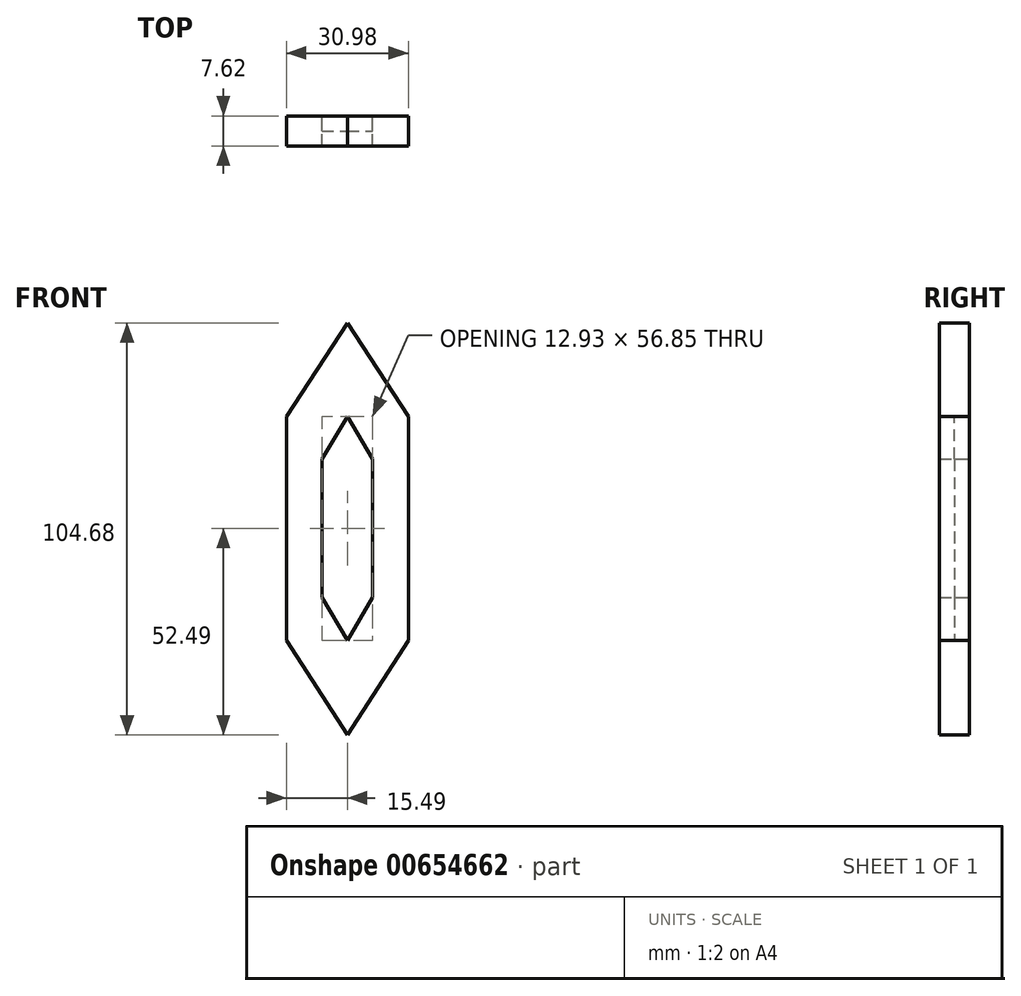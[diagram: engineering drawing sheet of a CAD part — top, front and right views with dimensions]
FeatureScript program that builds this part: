
annotation { "Feature Type Name" : "Feature", "Feature Type Description" : "" }
export const myFeature = defineFeature(function(context is Context, id is Id, definition is map)
    precondition{}
    {
        {
            var Q0;
            Q0=qCreatedBy(makeId("Front.planeOp"),FACE);
            var sketch = newSketch(context, id + "F0", { "sketchPlane" : qUnion([Q0])});
            skLineSegment(sketch, "E0.left", {"start": v(-15.5, 28.42) * mm, "end": v(-15.5, -28.42) * mm});
            skLineSegment(sketch, "E0.right", {"start": v(15.5, 28.42) * mm, "end": v(15.5, -28.42) * mm});
            skPoint(sketch, "E0.middle", {"position": v(0, 0) * mm});
            skLineSegment(sketch, "E1", {"start": v(-15.5, 28.42) * mm, "end": v(0, 52.19) * mm});
            skLineSegment(sketch, "E2", {"start": v(0, 52.19) * mm, "end": v(15.5, 28.42) * mm});
            skLineSegment(sketch, "E3", {"start": v(-15.5, -28.42) * mm, "end": v(0, -52.49) * mm});
            skLineSegment(sketch, "E4", {"start": v(0, -52.49) * mm, "end": v(15.5, -28.42) * mm});
            skLineSegment(sketch, "E5.left", {"start": v(-6.47, 17.6) * mm, "end": v(-6.47, -17.6) * mm});
            skLineSegment(sketch, "E5.right", {"start": v(6.47, 17.6) * mm, "end": v(6.47, -17.6) * mm});
            skLineSegment(sketch, "E6", {"start": v(-6.47, 17.6) * mm, "end": v(0, 28.42) * mm});
            skLineSegment(sketch, "E7", {"start": v(0, 28.42) * mm, "end": v(6.47, 17.6) * mm});
            skLineSegment(sketch, "E8", {"start": v(-6.47, -17.6) * mm, "end": v(0, -28.42) * mm});
            skLineSegment(sketch, "E9", {"start": v(0, -28.42) * mm, "end": v(6.47, -17.6) * mm});
            skLineSegment(sketch, "E10", {"start": v(-15.5, 0) * mm, "end": v(15.5, 0) * mm});
            skSolve(sketch);
        }
        {
            var Q0;
            Q0=makeQuery(id+"F0.imprint","IMPRINT",FACE,{"disambiguationData":[TD([[makeQuery(id+"F0.imprint","IMPRINT",EDGE,{"derivedFrom":sQuery(id+"F0.wireOp",EDGE,"E0.left")}),1.0]])]});
            extrude(context, id + "F1", {"entities" : qUnion([Q0]), "depth" : 7.62 * mm, "offsetDistance" : 25.4 * mm});
        }
        {
            var Q0;
            Q0=makeQuery(id+"F0.imprint","IMPRINT",FACE,{"disambiguationData":[TD([[makeQuery(id+"F0.imprint","IMPRINT",EDGE,{"derivedFrom":sQuery(id+"F0.wireOp",EDGE,"E5.left")}),1.0]])]});
            extrude(context, id + "F2", {"entities" : qUnion([Q0]), "depth" : 3.8 * mm, "offsetDistance" : 25.4 * mm});
        }
    });
